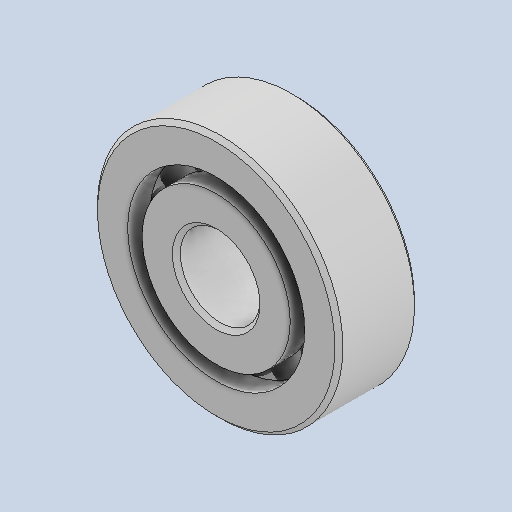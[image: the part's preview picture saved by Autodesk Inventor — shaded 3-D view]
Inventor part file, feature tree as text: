
AUTODESK INVENTOR PART (.ipt)
format: ipt  version: 2023 (Build 270158000, 158)  size: 574,976 bytes
history: native  units: in
note: dims shown in document units (in); Inventor stores cm internally (conversion verified against a paired STEP export)
features: other x11, revolve x3
ambient origin geometry x8: Origin, YZ Plane, XZ Plane, XY Plane, X Axis, Y Axis, Z Axis, Center Point
bodies: Solid1 (feature_tree), Solid2 (feature_tree), Solid3 (feature_tree), Solid4 (feature_tree), Solid5 (feature_tree), Solid6 (feature_tree), Solid7 (feature_tree), Solid8 (feature_tree), Solid9 (feature_tree), Solid10 (feature_tree), Solid11 (feature_tree), Solid12 (feature_tree), Solid13 (feature_tree), Solid14 (feature_tree)
feature tree (14):
  revolve  "Revolve1"  [1 undecoded]
  revolve  "Revolve3"  [1 undecoded]
  revolve  "Revolve4"  [1 undecoded]
  other  "CirPattern1[1]"
  other  "CirPattern1[2]"
  other  "CirPattern1[3]"
  other  "CirPattern1[4]"
  other  "CirPattern1[5]"
  other  "CirPattern1[6]"
  other  "CirPattern1[7]"
  other  "CirPattern1[8]"
  other  "CirPattern1[9]"
  other  "CirPattern1[10]"
  other  "CirPattern1[11]"
note: 3 required parameter values undecoded (feature->parameter linkage not recoverable at this tier; creation-order binding heuristic only, values carry confidence <= 0.55)
